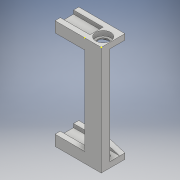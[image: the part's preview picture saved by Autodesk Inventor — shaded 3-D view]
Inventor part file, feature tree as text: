
AUTODESK INVENTOR PART (.ipt)
format: ipt  version: 2018 (Build 220112000, 112)  size: 272,896 bytes
history: native  units: mm
features: sketch x14, extrude x12, fillet x1
ambient origin geometry x8: Origin, YZ Plane, XZ Plane, XY Plane, X Axis, Y Axis, Z Axis, Center Point
bodies: Solid1 (feature_tree)
feature tree (27):
  extrude  "Extrusion1"  Depth=165.0mm
  extrude  "Extrusion2"  Depth=8.5mm
  extrude  "Extrusion3"  Depth=25.0mm TaperAngle=0.0deg
  extrude  "Extrusion4"  Depth=25.0mm
  extrude  "Extrusion5"  Depth=7.1mm
  extrude  "Extrusion6"  Depth=7.1mm TaperAngle=0.0deg
  fillet  "Fillet1"  Radius=5.0mm
  sketch  "Sketch7"  dims[d18=5.0mm d19=10.0mm d20=0.0mm]
  extrude  "Extrusion7"  Depth=10.0mm TaperAngle=0.0deg
  extrude  "Extrusion8"  Depth=2.0mm
  sketch  "Sketch10"  dims[d27=16.0mm d28=8.0mm]
  extrude  "Extrusion9"  Depth=7.1mm TaperAngle=0.0deg
  extrude  "Extrusion10"  Depth=8.0mm
  extrude  "Extrusion11"  Depth=16.0mm
  extrude  "Extrusion12"  Depth=16.0mm
  sketch  "Sketch1"  dims[d0=25.0mm d1=165.0mm]
  sketch  "Sketch2"  dims[d2=3.0mm d3=0.0mm d4=8.5mm]
  sketch  "Sketch3"  dims[d5=8.5mm d6=25.0mm d7=0.0mm]
  sketch  "Sketch4"  dims[d8=25.0mm d9=22.0mm]
  sketch  "Sketch5"  dims[d10=7.1mm d11=0.0mm d12=15.5mm]
  sketch  "Sketch6"  dims[d13=165.0mm d14=0.0mm d15=7.1mm d16=0.0mm d17=5.0mm]
  sketch  "Sketch8"  dims[d21=2.0mm d22=22.75mm]
  sketch  "Sketch9"  dims[d23=7.1mm d24=0.0mm d25=7.1mm d26=0.0mm]
  sketch  "Sketch11"  dims[d29=16.0mm d30=16.0mm]
  sketch  "Sketch12"  dims[d31=8.0mm d32=16.0mm]
  sketch  "Sketch13"  dims[d33=45.0mm d34=0.0mm]
  sketch  "Sketch14"  dims[d35=8.0mm d36=0.0mm d37=12.25mm d38=3.5mm d39=12.25mm d40=3.5mm d41=12.25mm d42=3.5mm d43=12.25mm d44=40.0mm d45=0.0mm d46=2.5mm d47=5.0mm d48=2.5mm d49=5.0mm d50=20.0mm d51=0.0mm]
